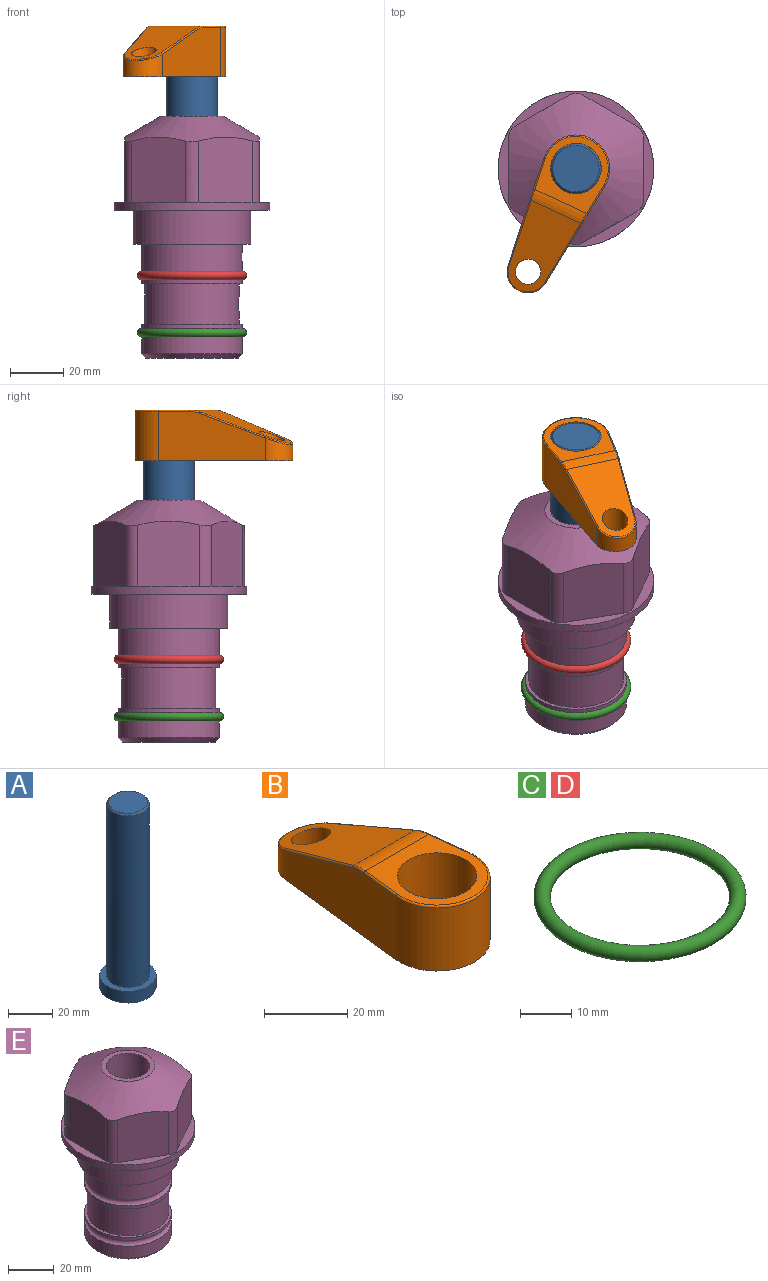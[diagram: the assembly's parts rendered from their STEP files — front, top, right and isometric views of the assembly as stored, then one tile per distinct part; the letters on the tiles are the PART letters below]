
ASSEMBLY  parts=5 mates=3
PART A: 6 faces, bbox 25.4x25.4x101.6 mm
  f0: plane 17.46x17.46mm, normal (0,0,1), area 239.5mm2, adj f5
  f1: plane 25.4x25.4mm, normal (0,0,-1), area 506.7mm2, adj f2
  f2: cylinder r=12.7mm len=25.4mm, axis (0,0,1), area 506.7mm2, adj f1,f3
  f3: plane 25.4x25.4mm, normal (0,0,1), area 221.7mm2, adj f2,f4
  f4: cylinder r=9.53mm len=94.46mm, axis (0,0,1), area 5653mm2, adj f3,f5
  f5: cone r=8.73mm half-angle=45deg, axis (0,0,-1), area 64.4mm2, adj f0,f4
PART B: 44 faces, bbox 27.5x64.5x19.1 mm
  f0: plane 2.3x0.95mm, normal (0,0,-1), area 1mm2, adj f25,f30,f34
  f1: plane 63.5x25.4mm, normal (0,0,-1), area 561.7mm2, adj f2,f3,f4,f5,f6,f7,f19,f20
  f2: cylinder r=12.7mm len=25.4mm, axis (0,0,-1), area 792.2mm2, adj f1,f3,f5,f13
  f3: plane 42.33x18.54mm, normal (0.99,0.11,0), area 647mm2, adj f1,f2,f4,f11,f12,f14
  f4: cylinder r=7.94mm len=15.78mm, axis (0,0,-1), area 158.6mm2, adj f1,f3,f5,f16
  f5: plane 42.33x18.54mm, normal (-0.99,0.11,0), area 647mm2, adj f1,f2,f4,f15,f17,f18
  f6: cylinder r=9.53mm len=19.05mm, axis (0,0,-1), area 1140.1mm2, adj f1,f8
  f7: cylinder r=4.76mm len=10.98mm, axis (0,0,-1), area 276.1mm2, adj f1,f9
  f8: plane 25.83x24.38mm, normal (0,0,1), area 262.2mm2, adj f6,f10,f11,f13,f15
  f9: plane 32.49x20.55mm, normal (0,0.34,0.94), area 489.9mm2, adj f7,f10,f14,f16,f18
  f10: cylinder r=12.7mm len=21.49mm, axis (-1,0,0), area 93.2mm2, adj f8,f9,f12,f17
  f11: cylinder r=0.51mm len=12.34mm, axis (0.11,-0.99,0), area 9.9mm2, adj f3,f8,f12,f13
  f12: bspline ~7.62x1.64mm, area 3.5mm2, adj f3,f10,f11,f14
  f13: torus R=12.19mm, axis (0,0,1), area 33.6mm2, adj f2,f8,f11,f15
  f14: cylinder r=0.51mm len=26.01mm, axis (0.1,-0.93,0.34), area 21.6mm2, adj f3,f9,f12,f16
  f15: cylinder r=0.51mm len=12.34mm, axis (0.11,0.99,0), area 9.9mm2, adj f5,f8,f13,f17
  f16: bspline ~15.78x7.05mm, area 15.7mm2, adj f4,f9,f14,f18
  f17: bspline ~7.62x1.64mm, area 3.5mm2, adj f5,f10,f15,f18
  f18: cylinder r=0.51mm len=26.01mm, axis (0.1,0.93,-0.34), area 21.6mm2, adj f5,f9,f16,f17
  f19: plane 21.6x14.29mm, normal (-0.99,-0.11,0), area 242.6mm2, adj f1,f26,f28,f34,f36,f38
  f20: plane 21.6x14.29mm, normal (0.99,-0.11,0), area 242.6mm2, adj f1,f27,f29,f37,f39,f41
  f21: cylinder r=12.7mm len=14.29mm, axis (0,0,-1), area 173.2mm2, adj f1,f26,f27,f30,f31,f33
  f22: cylinder r=7.94mm len=7.63mm, axis (0,0,-1), area 53.8mm2, adj f1,f28,f29,f42
  f23: plane 2.3x0.95mm, normal (0,0,-1), area 1mm2, adj f25,f33,f37
  f24: plane 17.94x12.32mm, normal (0,-0.34,-0.94), area 191.2mm2, adj f25,f38,f41,f42
  f25: cylinder r=9.53mm len=12.93mm, axis (-1,0,0), area 37.5mm2, adj f0,f23,f24,f31,f36,f39
  f26: cylinder r=1.59mm len=14.29mm, axis (0,0,-1), area 49mm2, adj f1,f19,f21,f32
  f27: cylinder r=1.59mm len=14.29mm, axis (0,0,-1), area 49mm2, adj f1,f20,f21,f35
  f28: cylinder r=1.59mm len=7.28mm, axis (0,0,-1), area 22.1mm2, adj f1,f19,f22,f40
  f29: cylinder r=1.59mm len=7.28mm, axis (0,0,-1), area 22.1mm2, adj f1,f20,f22,f43
  f30: torus R=14.29mm, axis (0,0,1), area 5.8mm2, adj f0,f21,f31,f32
  f31: bspline ~11.06x2.73mm, area 20.8mm2, adj f21,f25,f30,f33
  f32: sphere r=1.59mm, area 5.4mm2, adj f26,f30,f34
  f33: torus R=14.29mm, axis (0,0,1), area 5.8mm2, adj f21,f23,f31,f35
  f34: cylinder r=1.59mm len=1.68mm, axis (-0.11,0.99,0), area 2.4mm2, adj f0,f19,f32,f36
  f35: sphere r=1.59mm, area 5.4mm2, adj f27,f33,f37
  f36: bspline ~5.82x2.33mm, area 7.7mm2, adj f19,f25,f34,f38
  f37: cylinder r=1.59mm len=1.68mm, axis (0.11,0.99,0), area 2.4mm2, adj f20,f23,f35,f39
  f38: cylinder r=1.59mm len=18.33mm, axis (0.1,-0.93,0.34), area 46.7mm2, adj f19,f24,f36,f40
  f39: bspline ~5.82x2.33mm, area 7.7mm2, adj f20,f25,f37,f41
  f40: sphere r=1.59mm, area 3.6mm2, adj f28,f38,f42
  f41: cylinder r=1.59mm len=18.33mm, axis (0.1,0.93,-0.34), area 46.7mm2, adj f20,f24,f39,f43
  f42: bspline ~8.31x1.84mm, area 15.3mm2, adj f22,f24,f40,f43
  f43: sphere r=1.59mm, area 3.6mm2, adj f29,f41,f42
PART C: 1 faces, bbox 44.7x44.7x3.2 mm
  f0: torus R=19.05mm, axis (0,0,1), area 1193.9mm2
PART D: same geometry as C
PART E: 36 faces, bbox 58.7x58.7x91.2 mm
  f0: cylinder r=17.78mm len=35.56mm, axis (0,0,1), area 1670.8mm2, adj f23,f24,f31
  f1: cylinder r=19.05mm len=38.1mm, axis (0,0,1), area 1191.9mm2, adj f26,f27,f30
  f2: plane 58.66x58.66mm, normal (0,0,-1), area 1150.6mm2, adj f3,f28
  f3: cylinder r=29.33mm len=58.66mm, axis (0,0,-1), area 585.1mm2, adj f2,f4
  f4: plane 58.66x58.66mm, normal (0,0,1), area 475.9mm2, adj f3,f5,f6,f7,f8,f9,f10,f11
  f5: plane 24.5x20.32mm, normal (-0.5,0.87,0), area 562.8mm2, adj f4,f15,f16,f17
  f6: plane 24.5x20.32mm, normal (0.5,0.87,0), area 562.8mm2, adj f4,f14,f15,f17
  f7: plane 24.5x23.48mm, normal (1,0,0), area 562.8mm2, adj f4,f13,f14,f17
  f8: plane 24.5x20.32mm, normal (0.5,-0.87,0), area 562.8mm2, adj f4,f12,f13,f17
  f9: plane 24.5x20.32mm, normal (-0.5,-0.87,0), area 562.8mm2, adj f4,f11,f12,f17
  f10: plane 24.5x23.48mm, normal (-1,0,0), area 562.8mm2, adj f4,f11,f16,f17
  f11: cylinder r=5.08mm len=23.01mm, axis (0,0,-1), area 121.2mm2, adj f4,f9,f10,f17
  f12: cylinder r=5.08mm len=23.01mm, axis (0,0,-1), area 121.2mm2, adj f4,f8,f9,f17
  f13: cylinder r=5.08mm len=23.01mm, axis (0,0,-1), area 121.2mm2, adj f4,f7,f8,f17
  f14: cylinder r=5.08mm len=23.01mm, axis (0,0,-1), area 121.2mm2, adj f4,f6,f7,f17
  f15: cylinder r=5.08mm len=23.01mm, axis (0,0,-1), area 121.2mm2, adj f4,f5,f6,f17
  f16: cylinder r=5.08mm len=23.01mm, axis (0,0,-1), area 121.2mm2, adj f4,f5,f10,f17
  f17: cone r=11.73mm half-angle=60deg, axis (0,0,-1), area 2071.8mm2, adj f5,f6,f7,f8,f9,f10,f11,f12
  f18: plane 23.46x23.46mm, normal (0,0,1), area 147.4mm2, adj f17,f35
  f19: plane 34.93x34.93mm, normal (0,0,-1), area 958mm2, adj f29
  f20: cylinder r=19.05mm len=38.1mm, axis (0,0,1), area 760.1mm2, adj f21,f29
  f21: torus R=19.05mm, axis (0,0,1), area 565.3mm2, adj f20,f22
  f22: cylinder r=19.05mm len=38.1mm, axis (0,0,1), area 190mm2, adj f21,f23
  f23: plane 38.1x38.1mm, normal (0,0,1), area 146.9mm2, adj f0,f22
  f24: plane 38.1x38.1mm, normal (0,0,-1), area 146.9mm2, adj f0,f25
  f25: cylinder r=19.05mm len=38.1mm, axis (0,0,1), area 190mm2, adj f24,f26
  f26: torus R=19.05mm, axis (0,0,1), area 565.3mm2, adj f1,f25
  f27: plane 44.45x44.45mm, normal (0,0,-1), area 411.7mm2, adj f1,f28
  f28: cylinder r=22.23mm len=44.45mm, axis (0,0,1), area 1773.5mm2, adj f2,f27
  f29: cone r=19.05mm half-angle=45deg, axis (0,0,1), area 257.5mm2, adj f19,f20
  f30: cylinder r=3.17mm len=6.75mm, axis (-1,0,0), area 128mm2, adj f1,f33
  f31: cylinder r=3.17mm len=6.35mm, axis (-1,0,0), area 102.5mm2, adj f0,f33
  f32: plane 25.4x25.4mm, normal (0,0,1), area 506.7mm2, adj f33
  f33: cylinder r=12.7mm len=66.42mm, axis (0,0,-1), area 5236.2mm2, adj f30,f31,f32,f34
  f34: cone r=9.53mm half-angle=30deg, axis (0,0,-1), area 443.4mm2, adj f33,f35
  f35: cylinder r=9.53mm len=19.05mm, axis (0,0,-1), area 849mm2, adj f18,f34
PLACE A rot(axis=(0,0,-1),114.9deg) t=(0,0,-4.11)mm
PLACE B rot(axis=(0,0,1),155.1deg) t=(0,0,50.5)mm
PLACE C t=(0,0,-21.59)mm
PLACE D at identity
PLACE E at identity fixed
MATE fastened C.f0 <-> E.f0  axis (0,0,1) through (0,0,-46.1)mm
MATE cylindrical A.f2 <-> E.f0  axis (0,0,1) through (0,0,21.52)mm
MATE fastened B.f2 <-> A.f2  axis (0,0,1) through (0,0,69.55)mm
